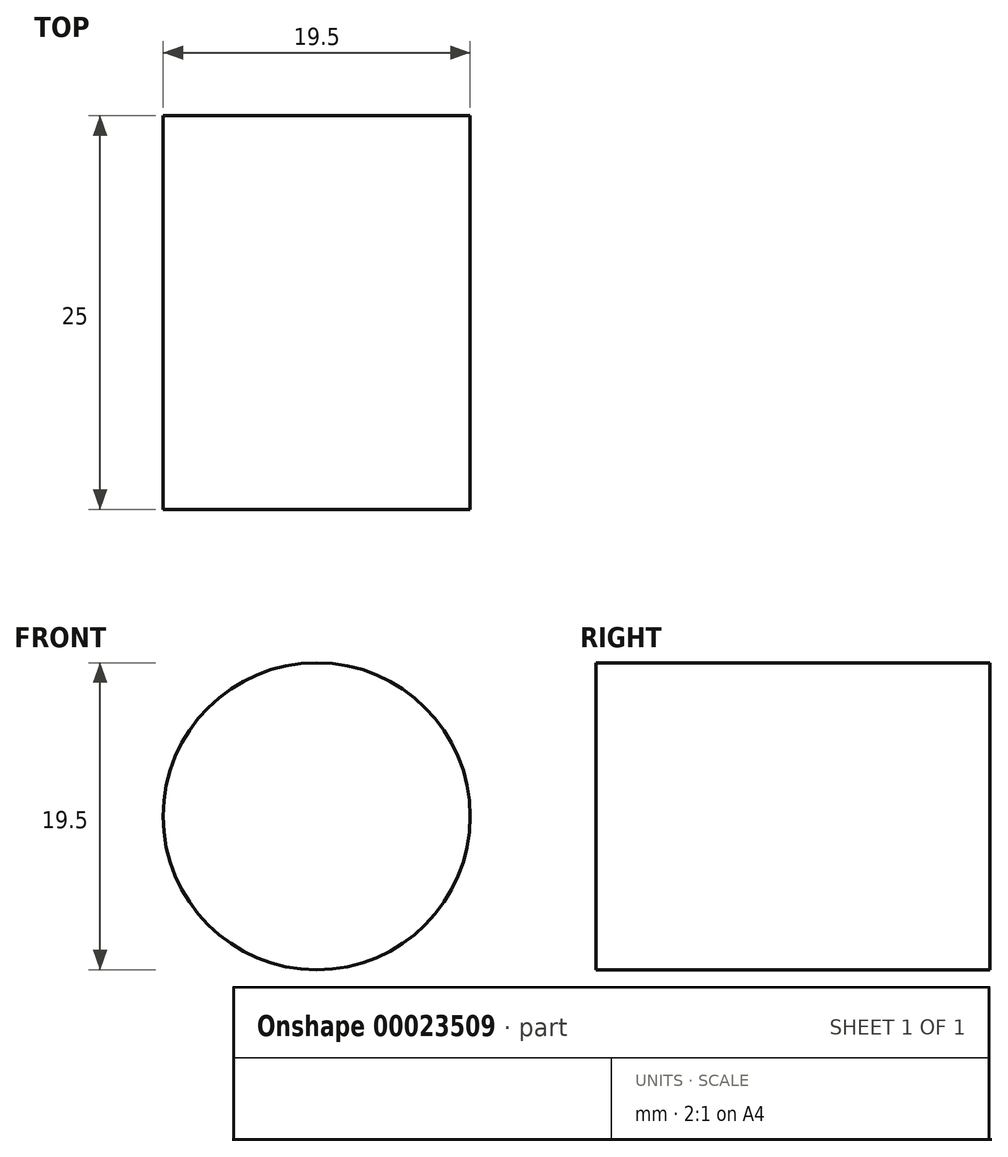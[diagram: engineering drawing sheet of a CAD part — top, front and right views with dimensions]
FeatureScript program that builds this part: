
annotation { "Feature Type Name" : "Feature", "Feature Type Description" : "" }
export const myFeature = defineFeature(function(context is Context, id is Id, definition is map)
    precondition{}
    {
        {
            var Q0;
            Q0=qCreatedBy(makeId("Front.planeOp"),FACE);
            var sketch = newSketch(context, id + "F0", { "sketchPlane" : qUnion([Q0])});
            skCircle(sketch, "E0", {"center": v(0, 0) * mm, "radius": 9.75 * mm});
            skSolve(sketch);
        }
        {
            var Q0;
            Q0=qSketchRegion(id+"F0",true);
            extrude(context, id + "F1", {"entities" : qUnion([Q0]), "depth" : 25 * mm});
        }
    });
